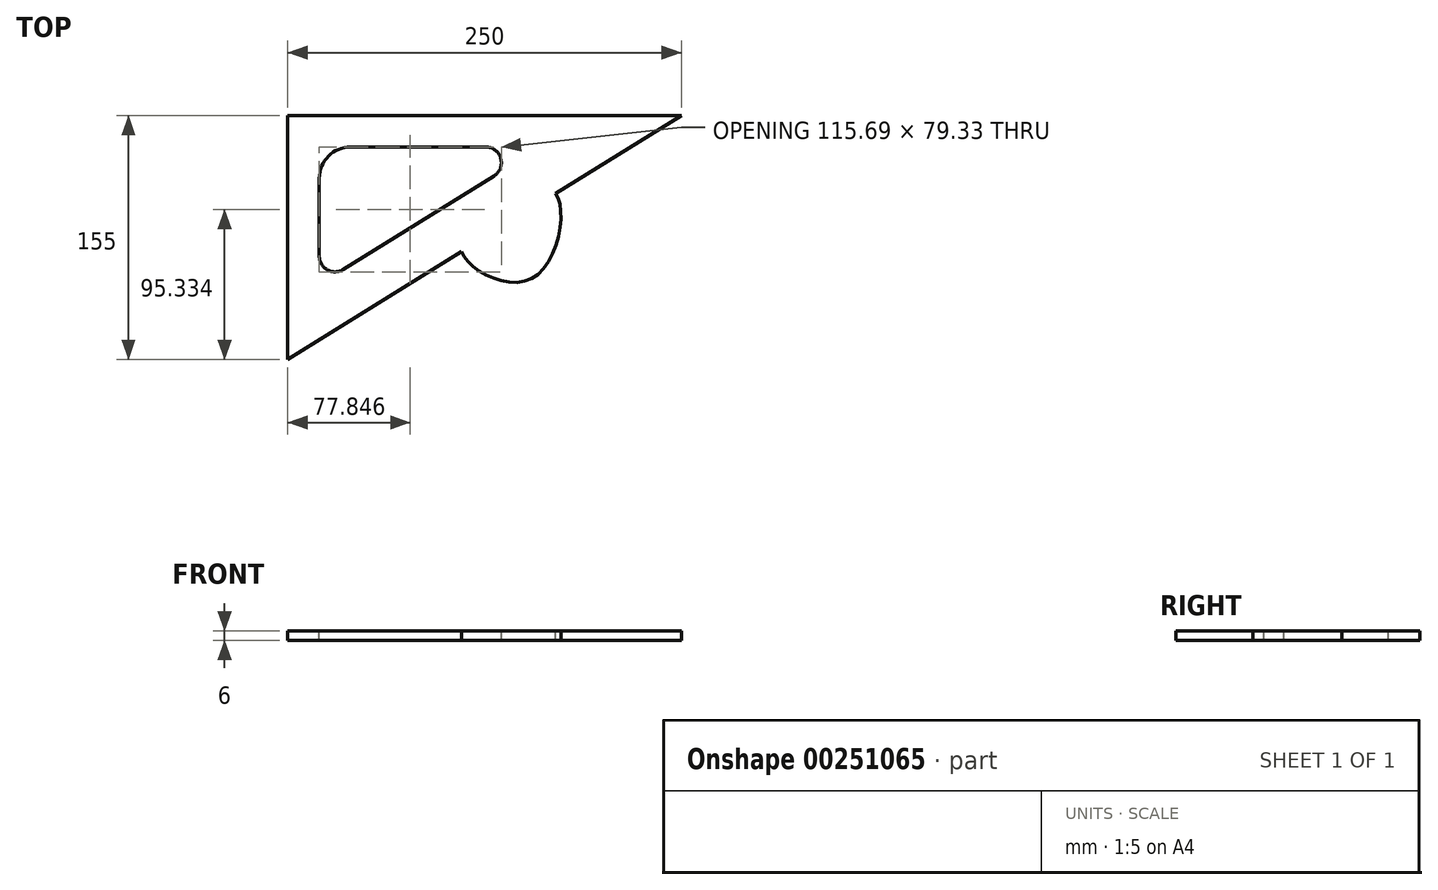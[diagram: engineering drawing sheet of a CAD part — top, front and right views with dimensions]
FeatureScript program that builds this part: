
annotation { "Feature Type Name" : "Feature", "Feature Type Description" : "" }
export const myFeature = defineFeature(function(context is Context, id is Id, definition is map)
    precondition{}
    {
        {
            var Q0;
            Q0=qCreatedBy(makeId("Top.planeOp"),FACE);
            var sketch = newSketch(context, id + "F0", { "sketchPlane" : qUnion([Q0])});
            skLineSegment(sketch, "E0", {"start": v(0, 0) * mm, "end": v(0, -155) * mm});
            skLineSegment(sketch, "E1", {"start": v(0, 0) * mm, "end": v(250, 0) * mm});
            skLineSegment(sketch, "E2", {"start": v(250, 0) * mm, "end": v(169.98, -49.61) * mm});
            skLineSegment(sketch, "E3", {"start": v(20, -40) * mm, "end": v(20, -89.34) * mm});
            skLineSegment(sketch, "E4", {"start": v(35.27, -97.83) * mm, "end": v(130.97, -38.5) * mm});
            skLineSegment(sketch, "E5", {"start": v(40, -20) * mm, "end": v(125.7, -20) * mm});
            skPoint(sketch, "E6.visualSharp", {"position": v(20, -20) * mm});
            skArc(sketch, "E6.filletArc", {"start": v(40, -20) * mm, "mid": v(25.86, -25.86) * mm, "end": v(20, -40) * mm});
            skPoint(sketch, "E7.visualSharp", {"position": v(160.8, -20) * mm});
            skArc(sketch, "E7.filletArc", {"start": v(130.97, -38.5) * mm, "mid": v(135.32, -27.26) * mm, "end": v(125.7, -20) * mm});
            skPoint(sketch, "E8.visualSharp", {"position": v(20, -107.3) * mm});
            skArc(sketch, "E8.filletArc", {"start": v(20, -89.34) * mm, "mid": v(25.14, -98.07) * mm, "end": v(35.27, -97.83) * mm});
            skFitSpline(sketch, "E9", {"points": [v(110.49, -86.5) * mm, v(132.6, -61.03) * mm, v(169.98, -49.61) * mm, v(155.16, -103.54) * mm, v(110.49, -86.5) * mm]});
            skLineSegment(sketch, "E10.trimOffspring", {"start": v(110.49, -86.5) * mm, "end": v(0, -155) * mm});
            skSolve(sketch);
        }
        {
            var Q0;
            Q0 = qSketchRegion(id + "F0", true);
            extrude(context, id + "F1", {"entities" : qUnion([Q0]), "oppositeDirection" : true, "depth" : 6 * mm});
        }
    });
